# Revit family: QF_MOFFAT_BLUESEAL_CE_GT45E
name_source: partatom
category: Specialty Equipment
revit_build: Autodesk Revit Architecture 2012 (Build: 20110916_2132(x64)
units: mm (PartAtom-declared; Revit-internal decimal feet)

## types (1)
- QF_MOFFAT_BLUESEAL_CE_GT45E
    Apparent Power = 115 VA
    Conn Conduit = Yes
    Cycle = 50 Hz
    Description = 450MM GAS FRYER WITH CONTROLLER SINGLE PAN
    FL Amps = 1 A
    Gas Connection Height = 0 mm  [stored 0 ft]
    Gas Input = 85300.0 Btu/h
    Gas KW = 25
    Gas Size = 1"
    Manufacturer = MOFFAT BLUESEAL
    Max Overcurrent Protection = 0 A
    Min Ckt Ampacity = 0 A
    Model = GT45E
    Phase = 1
    URL = www.moffat.com
    URL Cutsheet = www.moffat.com
    Volts = 230 V
    Watts = 115 W
    Weight in Pounds = 178

note: [stored X ft] marks values corroborated as IEEE doubles in the binary element streams (Revit-internal decimal feet)

## geometry (parser evidence)
native form markers: Blend x10, Sweep x3
no freeform markers — native parametric forms only
